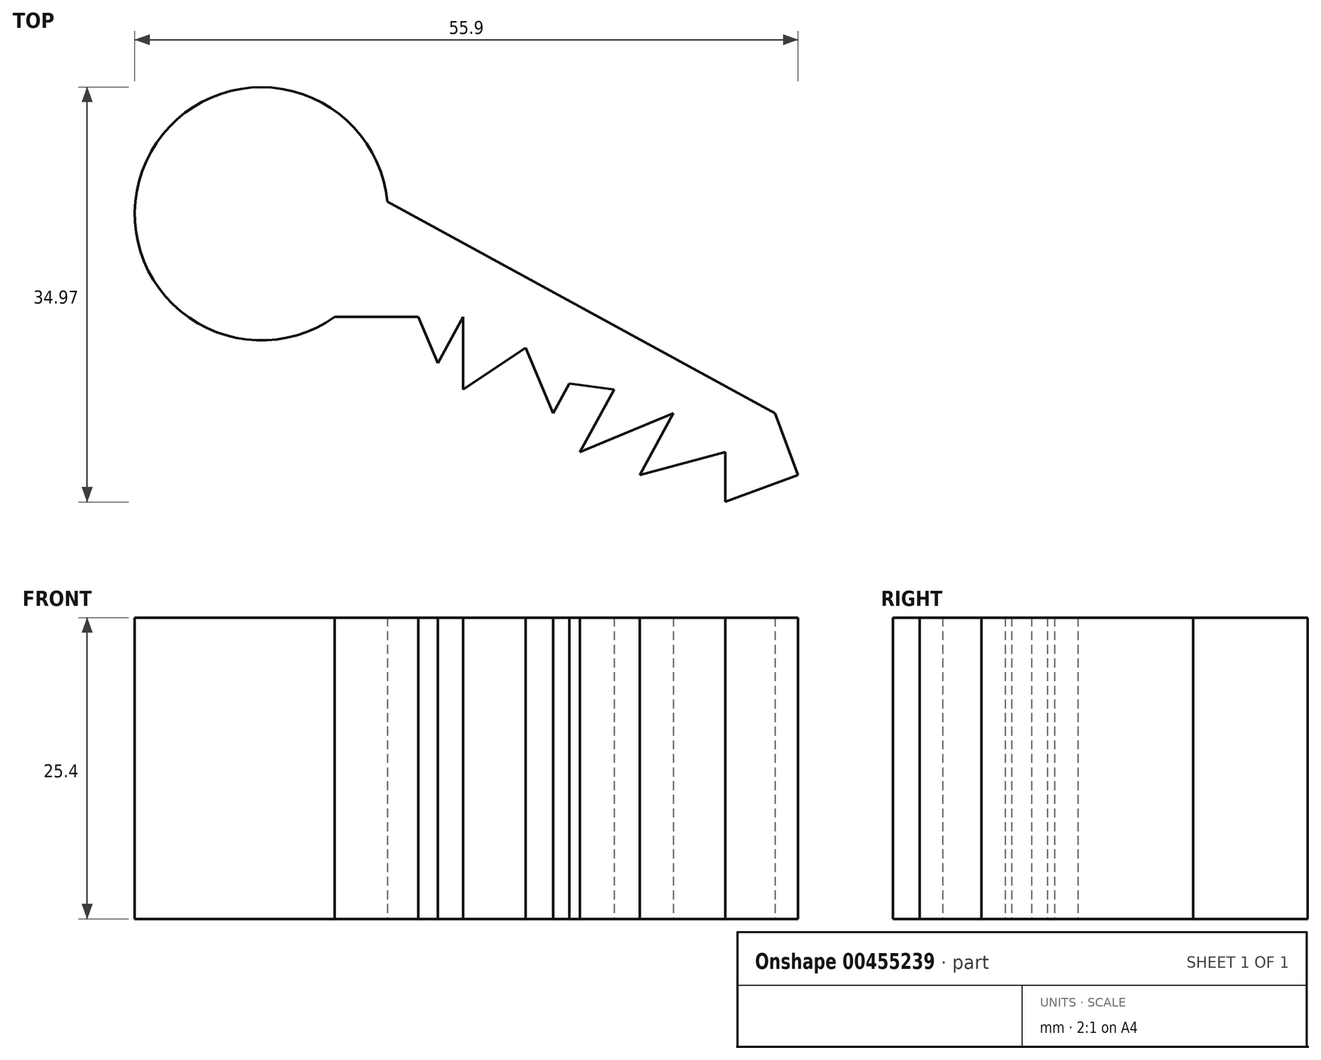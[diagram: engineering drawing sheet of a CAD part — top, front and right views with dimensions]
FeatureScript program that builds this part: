
annotation { "Feature Type Name" : "Feature", "Feature Type Description" : "" }
export const myFeature = defineFeature(function(context is Context, id is Id, definition is map)
    precondition{}
    {
        {
            var Q0;
            Q0=qCreatedBy(makeId("Top.planeOp"),FACE);
            var sketch = newSketch(context, id + "F0", { "sketchPlane" : qUnion([Q0])});
            skArc(sketch, "E0", {"start": v(-55.85, 36.14) * mm, "mid": v(-71.74, 49.27) * mm, "end": v(-51.41, 45.85) * mm});
            skLineSegment(sketch, "E1", {"start": v(-55.85, 36.14) * mm, "end": v(-53.53, 36.14) * mm});
            skLineSegment(sketch, "E2", {"start": v(-51.41, 45.85) * mm, "end": v(-18.75, 28.02) * mm});
            skLineSegment(sketch, "E3", {"start": v(-18.75, 28.02) * mm, "end": v(-16.81, 22.8) * mm});
            skLineSegment(sketch, "E4", {"start": v(-16.81, 22.8) * mm, "end": v(-22.93, 20.54) * mm});
            skLineSegment(sketch, "E5", {"start": v(-22.93, 20.54) * mm, "end": v(-22.93, 24.74) * mm});
            skLineSegment(sketch, "E6", {"start": v(-22.93, 24.74) * mm, "end": v(-30.15, 22.8) * mm});
            skLineSegment(sketch, "E7", {"start": v(-30.15, 22.8) * mm, "end": v(-27.3, 28.02) * mm});
            skLineSegment(sketch, "E8", {"start": v(-27.3, 28.02) * mm, "end": v(-35.17, 24.74) * mm});
            skLineSegment(sketch, "E9", {"start": v(-35.17, 24.74) * mm, "end": v(-32.3, 30.02) * mm});
            skLineSegment(sketch, "E10", {"start": v(-32.3, 30.02) * mm, "end": v(-36.08, 30.53) * mm});
            skLineSegment(sketch, "E11", {"start": v(-36.08, 30.53) * mm, "end": v(-37.45, 28.02) * mm});
            skLineSegment(sketch, "E12", {"start": v(-37.45, 28.02) * mm, "end": v(-39.76, 33.55) * mm});
            skLineSegment(sketch, "E13", {"start": v(-39.76, 33.55) * mm, "end": v(-45.03, 30.02) * mm});
            skLineSegment(sketch, "E14", {"start": v(-45.03, 30.02) * mm, "end": v(-45.03, 36.14) * mm});
            skLineSegment(sketch, "E15", {"start": v(-45.03, 36.14) * mm, "end": v(-47.17, 32.23) * mm});
            skLineSegment(sketch, "E16", {"start": v(-47.17, 32.23) * mm, "end": v(-48.8, 36.14) * mm});
            skLineSegment(sketch, "E17", {"start": v(-48.8, 36.14) * mm, "end": v(-53.53, 36.14) * mm});
            skSolve(sketch);
        }
        {
            var Q0;
            Q0 = qSketchRegion(id + "F0", true);
            extrude(context, id + "F1", {"entities" : qUnion([Q0]), "depth" : 25.4 * mm});
        }
    });
